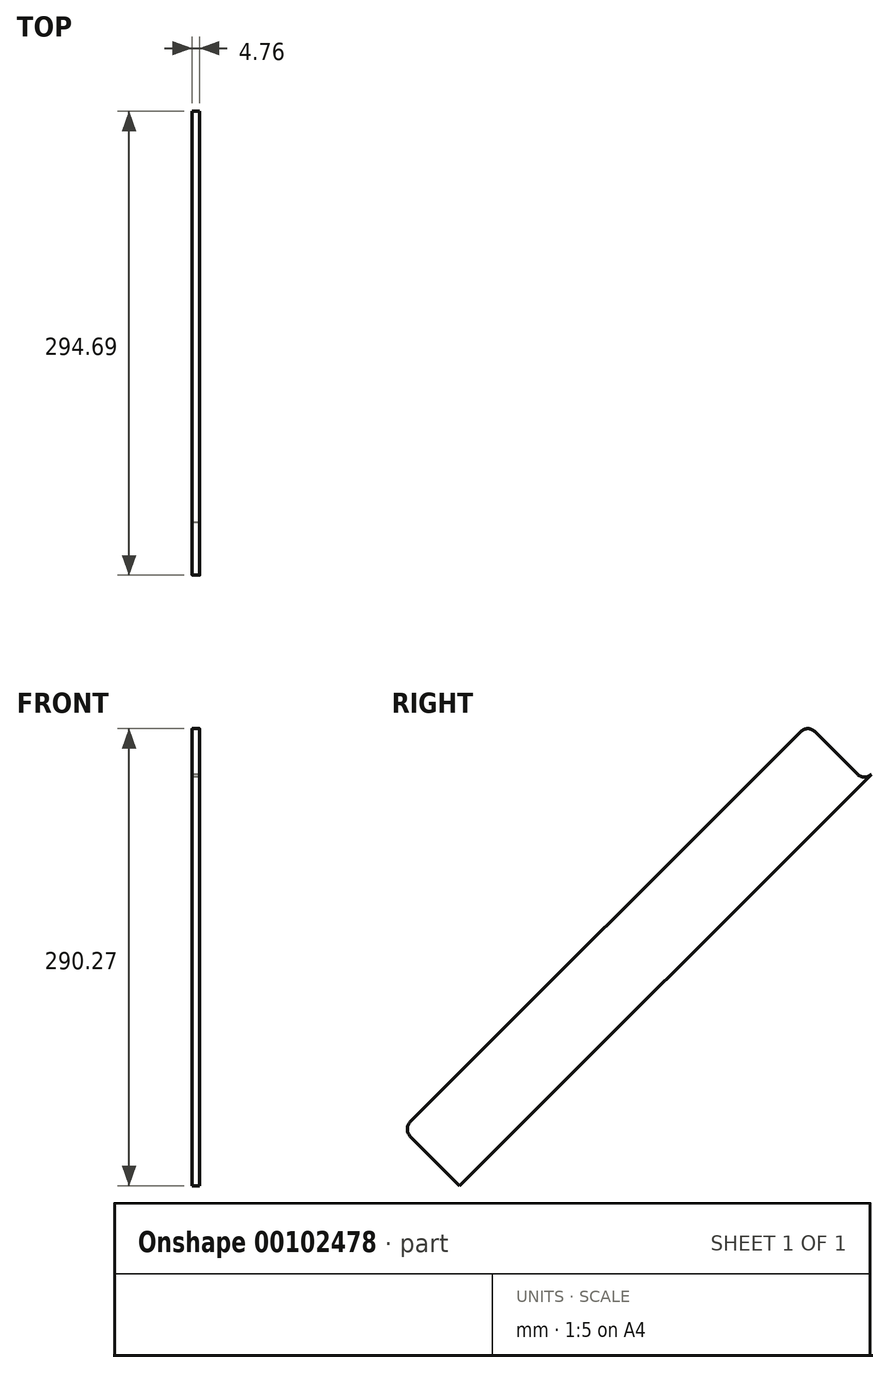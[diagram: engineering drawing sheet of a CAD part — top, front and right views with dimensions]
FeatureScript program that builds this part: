
annotation { "Feature Type Name" : "Feature", "Feature Type Description" : "" }
export const myFeature = defineFeature(function(context is Context, id is Id, definition is map)
    precondition{}
    {
        {
            var Q0;
            Q0=qCreatedBy(makeId("Right.planeOp"),FACE);
            var sketch = newSketch(context, id + "F0", { "sketchPlane" : qUnion([Q0])});
            skLineSegment(sketch, "E0", {"start": v(-19.1, 255.42) * mm, "end": v(-19.2, 255.52) * mm});
            skLineSegment(sketch, "E1", {"start": v(-271.7, -5.95) * mm, "end": v(-303.13, 25.48) * mm});
            skArc(sketch, "E2", {"start": v(-303.13, 34.46) * mm, "mid": v(-304.99, 29.97) * mm, "end": v(-303.13, 25.48) * mm});
            skLineSegment(sketch, "E3", {"start": v(-55.13, 282.46) * mm, "end": v(-303.13, 34.46) * mm});
            skLineSegment(sketch, "E4", {"start": v(-19.1, 255.42) * mm, "end": v(-46.15, 282.46) * mm});
            skArc(sketch, "E5", {"start": v(-46.15, 282.46) * mm, "mid": v(-50.64, 284.32) * mm, "end": v(-55.13, 282.46) * mm});
            skArc(sketch, "E6", {"start": v(-19.1, 255.42) * mm, "mid": v(-14.74, 253.56) * mm, "end": v(-10.3, 255.25) * mm});
            skLineSegment(sketch, "E7", {"start": v(-271.7, -5.95) * mm, "end": v(-10.3, 255.25) * mm});
            skSolve(sketch);
        }
        {
            var Q0;
            Q0 = qSketchRegion(id + "F0", true);
            extrude(context, id + "F1", {"entities" : qUnion([Q0]), "depth" : 4.76 * mm});
        }
    });
